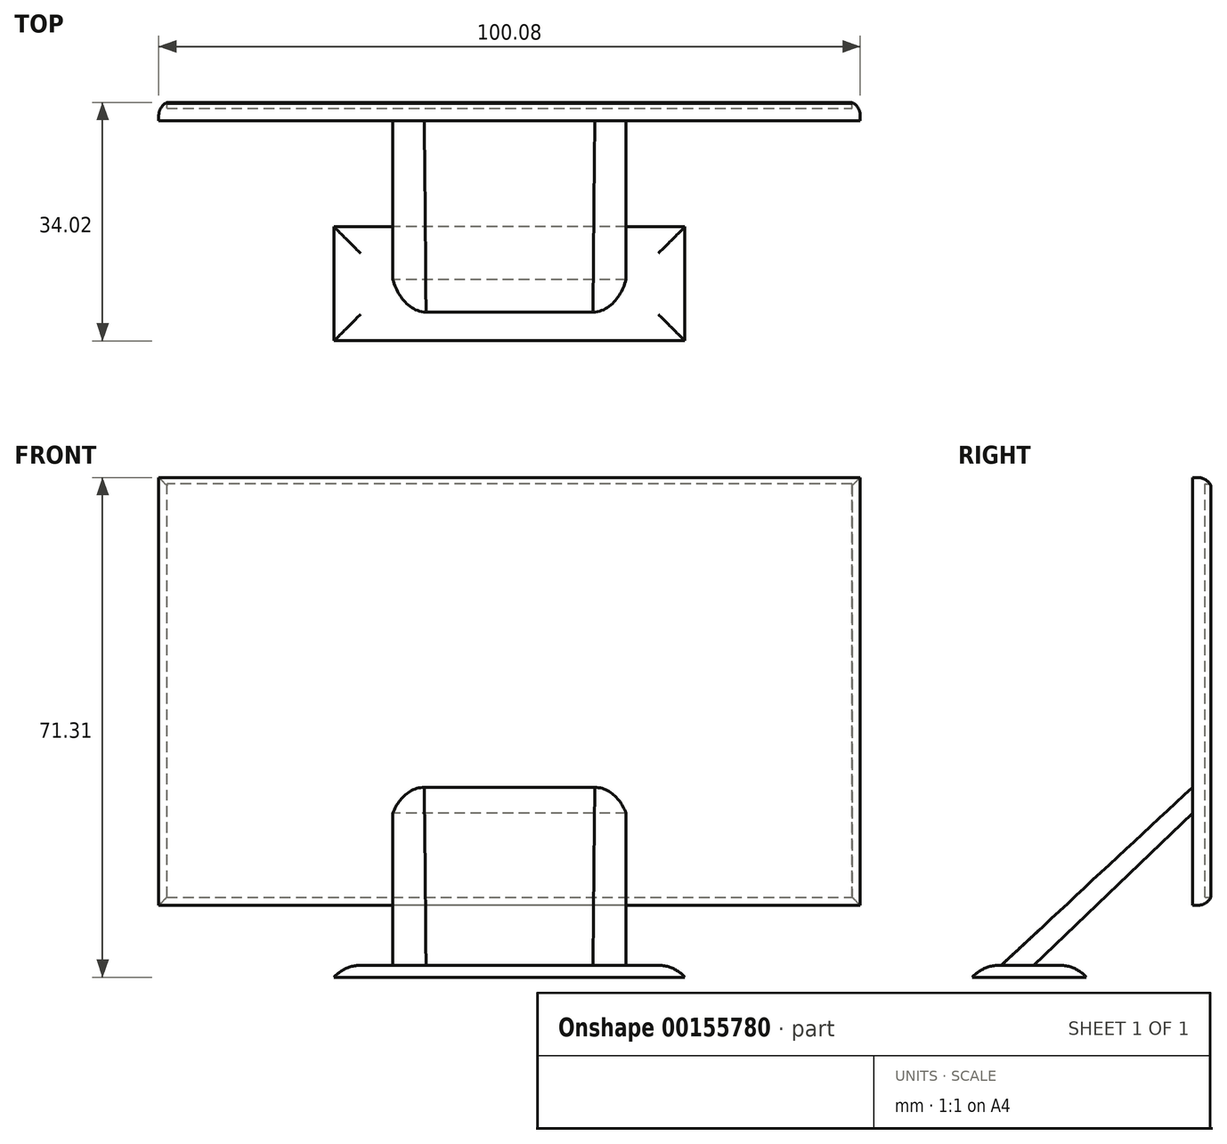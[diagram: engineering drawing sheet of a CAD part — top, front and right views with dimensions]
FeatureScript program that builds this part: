
annotation { "Feature Type Name" : "Feature", "Feature Type Description" : "" }
export const myFeature = defineFeature(function(context is Context, id is Id, definition is map)
    precondition{}
    {
        {
            var Q0;
            Q0=qCreatedBy(makeId("Right.planeOp"),FACE);
            var sketch = newSketch(context, id + "F0", { "sketchPlane" : qUnion([Q0])});
            skLineSegment(sketch, "E0.bottom", {"start": v(-3.43, -6.48) * mm, "end": v(-6.28, -6.48) * mm});
            skLineSegment(sketch, "E0.top", {"start": v(-3.43, 54.56) * mm, "end": v(-6.28, 54.56) * mm});
            skLineSegment(sketch, "E0.left", {"start": v(-3.43, -6.48) * mm, "end": v(-3.43, 54.56) * mm});
            skLineSegment(sketch, "E0.right", {"start": v(-6.28, -6.48) * mm, "end": v(-6.28, 54.56) * mm});
            skPoint(sketch, "E0.middle", {"position": v(-4.85, 24.04) * mm});
            skLineSegment(sketch, "E1", {"start": v(-6.28, 6.64) * mm, "end": v(-28.91, -15.04) * mm});
            skLineSegment(sketch, "E2", {"start": v(-28.91, -15.04) * mm, "end": v(-33.55, -15.04) * mm});
            skLineSegment(sketch, "E3", {"start": v(-33.55, -15.04) * mm, "end": v(-6.28, 10.35) * mm});
            skLineSegment(sketch, "E4.bottom", {"start": v(-21.4, -15.04) * mm, "end": v(-37.66, -15.04) * mm});
            skLineSegment(sketch, "E4.top", {"start": v(-21.4, -16.75) * mm, "end": v(-37.66, -16.75) * mm});
            skLineSegment(sketch, "E4.left", {"start": v(-21.4, -15.04) * mm, "end": v(-21.4, -16.75) * mm});
            skLineSegment(sketch, "E4.right", {"start": v(-37.66, -15.04) * mm, "end": v(-37.66, -16.75) * mm});
            skSolve(sketch);
        }
        {
            var Q0;
            {var subQ1=sQuery(id+"F0.wireOp",EDGE,"E0.bottom");Q0=makeQuery(id+"F0.imprint","IMPRINT",FACE,{"disambiguationData":[TD([[makeQuery(id+"F0.imprint","IMPRINT",EDGE,{"derivedFrom":subQ1}),-1.0]])]});}
            extrude(context, id + "F1", {"entities" : qUnion([Q0]), "endBound" : BoundingType.SYMMETRIC, "depth" : 100.08 * mm});
        }
        {
            var Q0;
            {var subQ0=sQuery(id+"F0.wireOp",EDGE,"E1");Q0=makeQuery(id+"F0.imprint","IMPRINT",FACE,{"disambiguationData":[TD([[makeQuery(id+"F0.imprint","IMPRINT",EDGE,{"derivedFrom":subQ0}),-1.0]])]});}
            extrude(context, id + "F2", {"entities" : qUnion([Q0]), "operationType" : NewBodyOperationType.ADD, "endBound" : BoundingType.SYMMETRIC, "depth" : 33.27 * mm});
        }
        {
            var Q0;
            Q0=makeQuery(id+"F0.imprint","IMPRINT",FACE,{"disambiguationData":[TD([[makeQuery(id+"F0.imprint","IMPRINT",EDGE,{"derivedFrom":sQuery(id+"F0.wireOp",EDGE,"E4.top")}),-1.0]])]});
            extrude(context, id + "F3", {"entities" : qUnion([Q0]), "operationType" : NewBodyOperationType.ADD, "endBound" : BoundingType.SYMMETRIC, "depth" : 50.04 * mm});
        }
        {
            var Q0;
            Q0=makeQuery(id+"F1.opExtrude","SWEPT_FACE",FACE,{"disambiguationData":[OSD([sQuery(id+"F0.wireOp",EDGE,"E0.left")])]});
            var sketch = newSketch(context, id + "F4", { "sketchPlane" : qUnion([Q0])});
            skLineSegment(sketch, "E5.bottom", {"start": v(48.87, -5.33) * mm, "end": v(-48.87, -5.33) * mm});
            skLineSegment(sketch, "E5.top", {"start": v(48.87, 53.67) * mm, "end": v(-48.87, 53.67) * mm});
            skLineSegment(sketch, "E5.left", {"start": v(48.87, -5.33) * mm, "end": v(48.87, 53.67) * mm});
            skLineSegment(sketch, "E5.right", {"start": v(-48.87, -5.33) * mm, "end": v(-48.87, 53.67) * mm});
            skPoint(sketch, "E5.middle", {"position": v(0, 24.17) * mm});
            skSolve(sketch);
        }
        {
            var Q0;
            Q0=makeQuery(id+"F1.opExtrude","CAP_EDGE",EDGE,{"disambiguationData":[OSD([sQuery(id+"F0.wireOp",EDGE,"E0.left")])],"isStart":false});
            var Q1;
            Q1=makeQuery(id+"F1.opExtrude","SWEPT_EDGE",EDGE,{"disambiguationData":[OSD([sQuery(id+"F0.wireOp",EDGE,"E0.top"),sQuery(id+"F0.wireOp",EDGE,"E0.left")])]});
            var Q2;
            Q2=makeQuery(id+"F1.opExtrude","CAP_EDGE",EDGE,{"disambiguationData":[OSD([sQuery(id+"F0.wireOp",EDGE,"E0.left")])],"isStart":true});
            var Q3;
            Q3=makeQuery(id+"F1.opExtrude","SWEPT_EDGE",EDGE,{"disambiguationData":[OSD([sQuery(id+"F0.wireOp",EDGE,"E0.bottom"),sQuery(id+"F0.wireOp",EDGE,"E0.left")])]});
            fillet(context, id + "F5", {"entities" : qUnion([Q0, Q1, Q2, Q3]), "radius" : 2.08 * mm, "tangentPropagation" : true, "allowEdgeOverflow" : false});
        }
        {
            var Q0;
            Q0=makeQuery(id+"F4.imprint","IMPRINT",FACE,{"disambiguationData":[TD([[makeQuery(id+"F4.imprint","IMPRINT",EDGE,{"derivedFrom":sQuery(id+"F4.wireOp",EDGE,"E5.bottom")}),-1.0]])]});
            extrude(context, id + "F6", {"entities" : qUnion([Q0]), "operationType" : NewBodyOperationType.REMOVE, "oppositeDirection" : true, "depth" : 1.04 * mm});
        }
        {
            var Q0;
            Q0=makeQuery(id+"F3.opExtrude","SWEPT_EDGE",EDGE,{"disambiguationData":[OSD([sQuery(id+"F0.wireOp",EDGE,"E4.bottom"),sQuery(id+"F0.wireOp",EDGE,"E4.right")])]});
            var Q1;
            Q1=makeQuery(id+"F3.opExtrude","CAP_EDGE",EDGE,{"disambiguationData":[OSD([sQuery(id+"F0.wireOp",EDGE,"E4.bottom")])],"isStart":false});
            var Q2;
            Q2=makeQuery(id+"F3.opExtrude","CAP_EDGE",EDGE,{"disambiguationData":[OSD([sQuery(id+"F0.wireOp",EDGE,"E4.bottom")])],"isStart":true});
            var Q3;
            Q3=makeQuery(id+"F3.opExtrude","SWEPT_EDGE",EDGE,{"disambiguationData":[OSD([sQuery(id+"F0.wireOp",EDGE,"E4.bottom"),sQuery(id+"F0.wireOp",EDGE,"E4.left")])]});
            var Q4;
            Q4=makeQuery(id+"F2.opExtrude","CAP_EDGE",EDGE,{"disambiguationData":[OSD([sQuery(id+"F0.wireOp",EDGE,"E3")])],"isStart":false});
            var Q5;
            Q5=makeQuery(id+"F2.opExtrude","CAP_EDGE",EDGE,{"disambiguationData":[OSD([sQuery(id+"F0.wireOp",EDGE,"E3")])],"isStart":true});
            fillet(context, id + "F7", {"entities" : qUnion([Q0, Q1, Q2, Q3, Q4, Q5]), "radius" : 5.08 * mm, "tangentPropagation" : true, "allowEdgeOverflow" : false});
        }
    });
